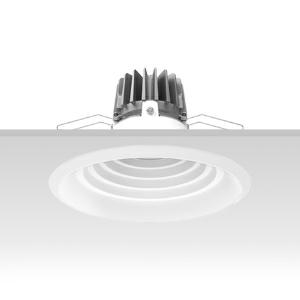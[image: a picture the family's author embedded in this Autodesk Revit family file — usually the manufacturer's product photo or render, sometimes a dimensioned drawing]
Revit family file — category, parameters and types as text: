
# Revit family: 3f_filippi_-_3f_reno_bianco_ugr_3f_filippi_-_30721_-_3f_reno_200_wh_2000-840_ugr
name_source: partatom
category: Lighting Fixtures
units: mm (PartAtom-declared; Revit-internal decimal feet)

## family parameters
Cut with Voids When Loaded = No
Host = Face
Light Source = No
Part Type = Normal
Room Calculation Point = No
Round Connector Dimension = Use Diameter
Shared = No

## types (1)
- 3F Filippi - 3F Reno Bianco UGR (1 x LED, 2458 lm, 20 W, 4000 K)
    Apparent Load = 20 VA
    Approval mark = CE
    CIE Flux Codes = 90 100 100 100 100
    Color Rendering = 80
    Color Temperature = 4000 K
    Control Gear = Electronic ballast
    Default Elevation = 1800 mm
    Description = ILLUMINOTECHNICAL
Luminous efficiency 100% (DLOR 100%, ULOR 0%).
Initial luminous flux of the luminaire 2458 lm.
Direct symmetric UGR distribution.
Installation Interdistance Transv.D = 0.99 x hu - Long.D = 1.01 x hu.
Average luminance <500 cd/m² for radial angles >65°.
Tabular UGR (CIE 117 - 4H-8H; S=0.25H; 70/50/20): RUG 17.4 - 17.3.
Beam angle: 64° - 65°.
Luminous efficacy 123 lm/W.
Lifetime (L90/B10): 30000 h. (tq+25°C)
Lifetime (L85/B10): 50000 h. (tq+25°C)
Lifetime (L70/B10): 80000 h. (tq+25°C)
Sudden decreased luminous flux after 50000 hours: 0% (C0).
Photobiological safety in compliance with IEC/TR 62778: RG0 risk exempt, (IEC 62471).
In compliance with IEC/EN 62722-2-1 - IEC/EN 62717 standards.

SOURCE
Compact LED module 2000/840.
Energy efficiency class (UE 2019/2020 - UE 2019/2015): D.
CIE 13.3 Colour rendering index: CRI >80 (R9 <50%).
IES TM-30 Fidelity Index: Rf = 84 Rg = 95.
CCT nominal colour temperature 4000 K.
Colour initial tolerance (MacAdam): SDCM 3.
Zhaga Book 3 compliant.

MECHANICAL
Passive heat dissipator in die-casting aluminium, oversized, for optimum thermal management of the LED module.
Parabolic element with graduated/concentric rings in white polycarbonate.
Internal specular metallic louvre to optimise control of the luminous flux in polycarbonate.
Transparent external lens with glossy and satin differentiated surfaces, with a cooling and anti-insect system in methacrylate (PMMA).
Fastening spring clips in stainless steel.
Dimensions: diameter 216 mm, height 142 mm. Weight 0.81 kg.
IP44 protection degree for exposed part, IP20 for recessed part.
Mechanical strength to impacts IK04 (0.5 joule).
Glow-wire test resistance 650°C.

ELECTRICAL
Wiring on a separate unit.
Halogen Free electronic wiring 230V-50/60Hz, power factor 0.95, THD <25%, constant output current, SELV, class II, 1 driver.
Power of the luminaire 20 W.
ENEC - CE.
SAFE FLICKER: PstLM=<1 and SVM=<0.4 (IEC TR 61547-1 and IEC TR 63158), to ensure a more comfortable and safe light.
Luminaire compliant with EN 60598-2-22 for power supply from a centralised emergency system CPSS (Central Power Supply System), not incorporated in the luminaire - high risk areas excluded. The default power and flux are 100% in AC and 100% in DC.
Ambient temperature from 0°C to +25°C.
Temperature class T6 max 85°C.
Relative humidity UR: <85%.

INSTALLATION
Pull-up recessed fitting.
False ceiling carving: 200 mm.
All accessories dedicated to this product are available on the Catalog and on our website www.3F-Filippi.com.

APPLICATIONS
In environments with VDTs, managerial offices and staterooms, public offices and schools.
In false ceilings with narrow voids.

WARNING
Luminaire designed for disposal/recycling at end-of-life.
Replaceable (LED only) light source by a professional. Replaceable control gear by a professional.
    Height = 0 mm  [stored 0 ft]
    Lamp = 1 x LED
    Lamp Light Flux = 2458 lm
    Lamp Power = 20 W
    Lamp count = 1
    Length = 216 mm
    Lifetime = 50000 h
    Luminous efficacy = 123 lm/W
    Manufacturer = 3F Filippi
    ModVariant = No
    Model = 3F Filippi - 30721 - 3F Reno 200 WH 2000-840 UGR
    Mounting Place = Ceiling
    Mounting Type = Recessed
    Number of Poles = 1
    OnlyDefault = Yes
    Power Factor = 1
    Product Name = 3F Filippi - 3F Reno Bianco UGR
    Product group = recessed luminaire
    ProductGroupID = 4
    Protection Class = Protection class II
    Protection Degree = IP 20
    RLX_Detail_Level = 1
    RLX_Emergency_Light_Flux = 0 lm
    RLX_Emergency_Type = 0
    RLX_Emergency_Type_DB = No
    RlxData = <blob elided: 88237 chars, md5=bd4cbc0b>
    Socket = socket
    Standby Power = 0 W
    System Light Flux = 2458 lm
    System Power = 20 W
    Type Comments = Product without accessories
    Type Image = 3ffilippi_3f_reno_200_wh_2000.jpg
    URL = http://relux.com
    VarID = ---
    Voltage = 0 V
    Weight = 0.00 kg
    Width = 0 mm  [stored 0 ft]

note: [stored X ft] marks values corroborated as IEEE doubles in the binary element streams (Revit-internal decimal feet)

## geometry (parser evidence)
native form markers: Blend x4, Sweep x11
no freeform markers — native parametric forms only
